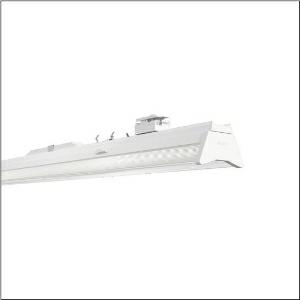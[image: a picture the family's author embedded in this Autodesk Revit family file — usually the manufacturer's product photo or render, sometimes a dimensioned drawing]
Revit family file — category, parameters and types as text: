
# Revit family: licross_11_performance_mo_51td167n485g
name_source: partatom
category: Lighting Fixtures
units: mm (PartAtom-declared; Revit-internal decimal feet)

## family parameters
Cut with Voids When Loaded = No
Host = Face
Light Source = No
Part Type = Normal
Room Calculation Point = No
Round Connector Dimension = Use Diameter
Shared = No

## types (1)
- Licross 11 Performance MO (1 x LED, 8840 lm, 48.6 W, 4000K)
    Apparent Load = 49 VA
    CIE Flux Codes = 66 88 96 79 100
    Color Rendering = 80
    Color Temperature = 4000K
    Default Elevation = 1800 mm
    Description = Licross 11 Performance MO, luminaire insert, of sheet steel, galvanised, coil coated, white, length: 1.500mm, width: 120mm, height: 123mm, LED rated luminous flux: 8.840lm, light colour: 840, SDCM (Standard Deviation of Colour Matching)MacAdam ≤ 2 SDCM (initial), control gear: ON/OFF, with plug, 3-pole, with phase selection, mains connection: 220..240V, AC, 50/60Hz, rated input power: 49W, internal wiring halogen-free, primary light control with lens, of plastic, primary optical cover: cover, of PMMA, light emission: direct/indirect distribution, primary light characteristic: symmetric, protection rating (complete): IP54, insulation class (complete): insulation class I (protective earthing), certification: CE, ENEC, VDE, UKCA, protection symbol: D if used in an environment with non-conductive dust loads with corresponding accessories, impact resistance: IK06, permissible ambient temperature for indoor applications: -25..+35°C, corresponds to IFS (International Featured Standards) requirements for safety and quality in the food industry, reducing of maximum allowable ambient temperature of 5°C with ceiling mounting, LABS conformity tested according to VDMA 24364:2018-05, The light source and the operating device comply with the requirements of the Ecodesign Regulation (EU) 2019/2020 and are replaceable in accordance with this regulation, packaging unit: 1 piece
    Height = 114 mm
    Lamp = 1 x LED
    Lamp Light Flux = 8840 lm
    Lamp Power = 48.6 W
    Lamp count = 1
    Length = 1500 mm
    Luminous efficacy = 182 lm/W
    Manufacturer = Siteco
    ModVariant = No
    Model = 51TD167N485G
    Mounting Place = Ceiling
    Mounting Type = Pendant
    Number of Poles = 1
    OnlyDefault = Yes
    Power Factor = 1
    Product Name = Licross 11 Performance MO
    Product group = luminaire insert | ceiling pendant
    ProductGroupID = 901
    Protection Class = Protection class I
    Protection Degree = IP 54
    RLX_Detail_Level = 1
    RLX_Emergency_Light_Flux = 0 lm
    RLX_Emergency_Type = 0
    RLX_Emergency_Type_DB = No
    RlxData = <blob elided: 30697 chars, md5=9bd06c7e>
    Socket = socket
    Standby Power = 0 W
    System Light Flux = 8840 lm
    System Power = 49 W
    Type Comments = Product without accessories
    Type Image = l_1256138.jpg
    URL = http://relux.com
    VarID = ---
    Voltage = 0 V
    Weight = 0.00 kg
    Width = 120 mm

## geometry (parser evidence)
native form markers: Blend x4, Sweep x12
no freeform markers — native parametric forms only
